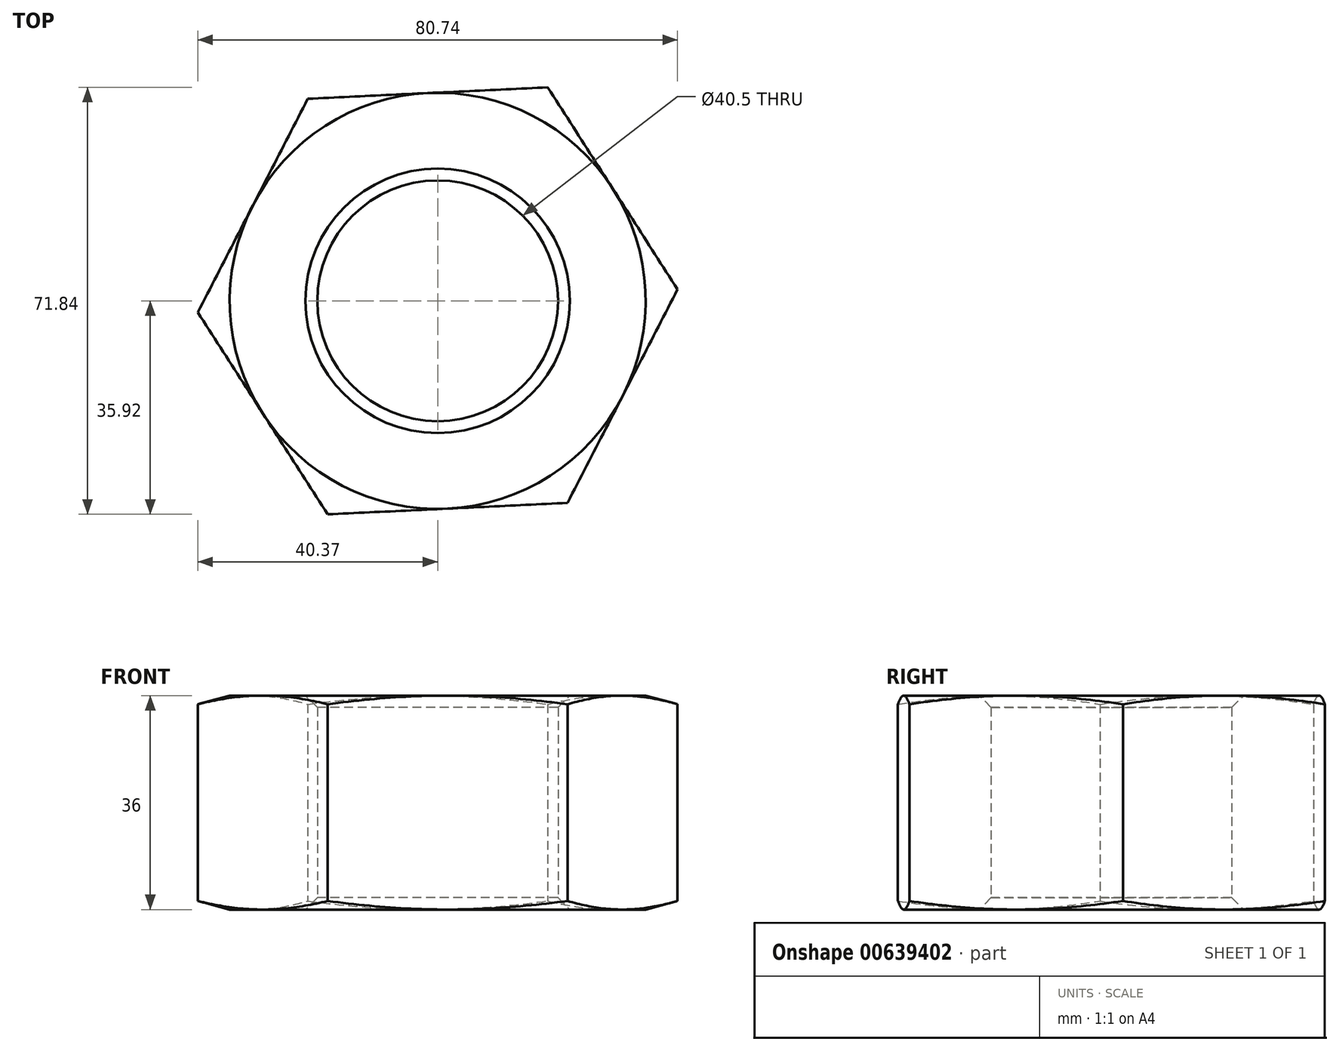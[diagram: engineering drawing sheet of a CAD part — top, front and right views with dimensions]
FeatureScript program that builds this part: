
annotation { "Feature Type Name" : "Feature", "Feature Type Description" : "" }
export const myFeature = defineFeature(function(context is Context, id is Id, definition is map)
    precondition{}
    {
        {
            var Q0;
            Q0=qCreatedBy(makeId("Top.planeOp"),FACE);
            var sketch = newSketch(context, id + "F0", { "sketchPlane" : qUnion([Q0])});
            skCircle(sketch, "E0.cCircle", {"center": v(0, 0) * mm, "radius": 35 * mm, "construction": true});
            skLineSegment(sketch, "E0.0", {"start": v(40.37, 1.93) * mm, "end": v(21.85, -34) * mm});
            skLineSegment(sketch, "E0.1", {"start": v(21.85, -34) * mm, "end": v(-18.51, -35.92) * mm});
            skLineSegment(sketch, "E0.2", {"start": v(-18.51, -35.92) * mm, "end": v(-40.37, -1.93) * mm});
            skLineSegment(sketch, "E0.3", {"start": v(-40.37, -1.93) * mm, "end": v(-21.85, 34) * mm});
            skLineSegment(sketch, "E0.4", {"start": v(-21.85, 34) * mm, "end": v(18.51, 35.92) * mm});
            skLineSegment(sketch, "E0.5", {"start": v(18.51, 35.92) * mm, "end": v(40.37, 1.93) * mm});
            skPoint(sketch, "E0.0.midPoint", {"position": v(31.11, -16.03) * mm});
            skCircle(sketch, "E1", {"center": v(0, 0) * mm, "radius": 20.25 * mm});
            skSolve(sketch);
        }
        {
            var Q0;
            Q0=makeQuery(id+"F0.imprint","IMPRINT",FACE,{"disambiguationData":[TD([[makeQuery(id+"F0.imprint","IMPRINT",EDGE,{"derivedFrom":sQuery(id+"F0.wireOp",EDGE,"E0.0")}),-1.0]])]});
            extrude(context, id + "F1", {"entities" : qUnion([Q0]), "depth" : 36 * mm, "offsetDistance" : 25 * mm});
        }
        {
            var Q0;
            Q0=makeQuery(id+"F1.opExtrude","CAP_EDGE",EDGE,{"disambiguationData":[OSD([sQuery(id+"F0.wireOp",EDGE,"E1")])],"isStart":false});
            var Q1;
            Q1=makeQuery(id+"F1.opExtrude","CAP_EDGE",EDGE,{"disambiguationData":[OSD([sQuery(id+"F0.wireOp",EDGE,"E1")])],"isStart":true});
            chamfer(context, id + "F2", {"entities" : qUnion([Q0, Q1]), "width" : 2 * mm, "tangentPropagation" : true});
        }
        {
            var Q0;
            Q0=makeQuery(id+"F1.opExtrude","CAP_FACE",FACE,{"disambiguationData":[OSD([sQuery(id+"F0.wireOp",EDGE,"E0.0"),sQuery(id+"F0.wireOp",EDGE,"E0.1"),sQuery(id+"F0.wireOp",EDGE,"E0.2"),sQuery(id+"F0.wireOp",EDGE,"E0.3"),sQuery(id+"F0.wireOp",EDGE,"E0.4"),sQuery(id+"F0.wireOp",EDGE,"E0.5"),sQuery(id+"F0.wireOp",EDGE,"E1")])],"isStart":false});
            var sketch = newSketch(context, id + "F3", { "sketchPlane" : qUnion([Q0])});
            skCircle(sketch, "E2", {"center": v(0, 0) * mm, "radius": 35 * mm});
            skSolve(sketch);
        }
        {
            var Q0;
            Q0=makeQuery(id+"F1.opExtrude","CAP_VERTEX",VERTEX,{"disambiguationData":[OSD([sQuery(id+"F0.wireOp",EDGE,"E0.0"),sQuery(id+"F0.wireOp",EDGE,"E0.5")])],"isStart":false});
            var Q1;
            Q1=makeQuery(id+"F1.opExtrude","CAP_VERTEX",VERTEX,{"disambiguationData":[OSD([sQuery(id+"F0.wireOp",EDGE,"E0.0"),sQuery(id+"F0.wireOp",EDGE,"E0.5")])],"isStart":true});
            var Q2;
            Q2=makeQuery(id+"F1.opExtrude","CAP_VERTEX",VERTEX,{"disambiguationData":[OSD([sQuery(id+"F0.wireOp",EDGE,"E0.2"),sQuery(id+"F0.wireOp",EDGE,"E0.3")])],"isStart":false});
            cPlane(context, id + "F4", {"entities" : qUnion([Q0, Q1, Q2]), "cplaneType" : CPlaneType.THREE_POINT, "offset" : 25 * mm, "width" : 150 * mm, "height" : 150 * mm});
        }
        {
            var Q0;
            Q0=qCreatedBy(id+"F4.planeOp",FACE);
            var sketch = newSketch(context, id + "F5", { "sketchPlane" : qUnion([Q0])});
            skLineSegment(sketch, "E3.0", {"start": v(-35, 36) * mm, "end": v(35, 36) * mm});
            skLineSegment(sketch, "E4", {"start": v(35, 36) * mm, "end": v(44.66, 33.41) * mm});
            skLineSegment(sketch, "E5", {"start": v(44.66, 33.41) * mm, "end": v(44.66, 39.68) * mm});
            skLineSegment(sketch, "E6", {"start": v(44.66, 39.68) * mm, "end": v(35, 37.1) * mm});
            skLineSegment(sketch, "E7", {"start": v(35, 37.1) * mm, "end": v(35, 36) * mm});
            skPoint(sketch, "E8.0", {"position": v(40.41, 18) * mm});
            skLineSegment(sketch, "E9", {"start": v(40.41, 18) * mm, "end": v(22.78, 18) * mm});
            skLineSegment(sketch, "E10.MirrorCS", {"start": v(44.66, -3.68) * mm, "end": v(35, -1.1) * mm});
            skLineSegment(sketch, "E11.MirrorCS", {"start": v(44.66, 2.59) * mm, "end": v(44.66, -3.68) * mm});
            skLineSegment(sketch, "E12.MirrorCS", {"start": v(35, 0) * mm, "end": v(44.66, 2.59) * mm});
            skLineSegment(sketch, "E13.MirrorCS", {"start": v(35, -1.1) * mm, "end": v(35, 0) * mm});
            skSolve(sketch);
        }
        {
            var Q0;
            Q0=makeQuery(id+"F5.imprint","IMPRINT",FACE,{"disambiguationData":[TD([[makeQuery(id+"F5.imprint","IMPRINT",EDGE,{"derivedFrom":sQuery(id+"F5.wireOp",EDGE,"E4")}),1.0]])]});
            var Q1;
            Q1=makeQuery(id+"F5.imprint","IMPRINT",FACE,{"disambiguationData":[TD([[makeQuery(id+"F5.imprint","IMPRINT",EDGE,{"derivedFrom":sQuery(id+"F5.wireOp",EDGE,"E10.MirrorCS")}),-1.0]])]});
            var Q2;
            Q2=makeQuery(id+"F1.opExtrude","SWEPT_FACE",FACE,{"disambiguationData":[OSD([sQuery(id+"F0.wireOp",EDGE,"E1")])]});
            revolve(context, id + "F6", {"operationType" : NewBodyOperationType.REMOVE, "entities" : qUnion([Q0, Q1]), "axis" : qUnion([Q2]), "revolveType" : RevolveType.FULL, "oppositeDirection" : true});
        }
    });
